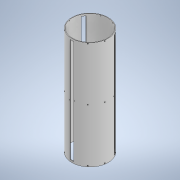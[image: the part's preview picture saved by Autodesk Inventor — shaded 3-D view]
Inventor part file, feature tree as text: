
AUTODESK INVENTOR PART (.ipt)
format: ipt  version: 2021 (Build 250183000, 183)  size: 350,208 bytes
history: native  units: in
note: dims shown in document units (in); Inventor stores cm internally (conversion verified against a paired STEP export)
features: other x34, hole x11, pattern_circular x8, sketch x8, plane x5, extrude x2
ambient origin geometry x8: Origin, YZ Plane, XZ Plane, XY Plane, X Axis, Y Axis, Z Axis, Center Point
bodies: Solid1 (feature_tree)
feature tree (68):
  extrude  "Extrusion1"  Depth=0.3937in
  plane  "Work Plane1"
  extrude  "Extrusion2"  Depth=0.3937in TaperAngle=0.0deg
  pattern_circular  "Circular Pattern1"  Count=3 Angle=360.0deg
  other  "Work Axis1"
  other  "Work Axis2"
  other  "Work Axis3"
  other  "Work Axis4"
  other  "Work Point1"
  other  "Work Point2"
  other  "Work Point3"
  other  "Central Plane"
  other  "Work Point4"
  other  "Work Axis6"
  other  "Work Axis7"
  other  "Offset Plane A"
  other  "Work Point5"
  other  "Work Point6"
  other  "Work Axis8"
  other  "Work Axis9"
  other  "Work Point7"
  other  "Work Point8"
  plane  "Work Plane5"
  plane  "Work Plane6"
  hole  "Hole1"  [1 undecoded]
  hole  "Hole2"  [1 undecoded]
  pattern_circular  "Circular Pattern3"  Count=3 Angle=360.0deg
  sketch  "Sketch5"  dims[d13=0.0484in d14=-11.811in]
  plane  "Work Plane7"
  sketch  "Sketch6"  dims[d15=0.0484in d16=0.1574in]
  hole  "Hole3"  [1 undecoded]
  other  "Work Axis10"
  hole  "Hole4"  [1 undecoded]
  pattern_circular  "Circular Pattern5"  Angle=60.0deg  [1 undecoded]
  plane  "Work Plane12"
  hole  "Hole5"  [1 undecoded]
  pattern_circular  "Circular Pattern6"  [2 undecoded]
  other  "plane for insert hole 1"
  sketch  "Sketch7"  dims[d17=-0.1574in]
  other  "plane for insert hole 2"
  sketch  "Sketch8"  dims[d48=1.0in d49=1.0in d29=0.096in d30=0.75in d31=0.185in d32=0.25in d33=0.5635in d34=1.0in d35=0.0in]
  hole  "insert hole 2"  [1 undecoded]
  hole  "insert hole 1"  [1 undecoded]
  pattern_circular  "Circular Pattern7"  [2 undecoded]
  pattern_circular  "Circular Pattern9"  [2 undecoded]
  other  "Work Axis14"
  other  "Work Axis16"
  other  "Work Point11"
  other  "Work Point12"
  other  "cap hardware plane 1"
  other  "cap hardware plane 2"
  sketch  "Sketch9"  dims[d52=1.0in d53=1.0in d38=0.096in d39=0.75in d40=0.185in d41=0.25in d42=0.5635in d43=1.0in d44=0.8108in d45=1.1811in d46=360.0deg]
  sketch  "Sketch10"  dims[d51=0.38in d54=0.177in d55=0.328in d56=0.332in d57=0.25in d58=0.5635in d59=0.484in d60=0.8108in d64=0.19in d65=0.177in d66=0.3229in d67=0.332in d68=0.25in d69=0.5635in d70=0.484in d71=0.8108in d72=1.5748in d73=360.0deg d75=60.0deg d76=1.0in d77=1.0in d78=0.129in d79=0.3229in d80=0.225in d81=0.25in d82=0.5635in d83=0.484in d84=0.8108in d85=1.1811in d86=360.0deg d88=0.2749in d89=0.2749in d90=0.0in d91=0.0in d92=0.0in d93=11.811in d94=0.0in d95=11.811in d96=0.129in d97=0.224in d98=0.225in d99=0.25in d100=0.5635in d101=0.349in d102=0.8108in d103=0.129in d104=0.224in d105=0.225in d106=0.25in d107=0.5635in d108=0.349in d109=0.8108in d110=1.1811in d111=360.0deg d116=1.1811in d117=360.0deg d119=0.0in d120=30.0deg d121=30.0deg d124=0.1969in d125=23.4252in d126=0.0in d127=0.0in d128=0.1969in d129=23.4252in d147=15.0deg d148=15.0deg d149=0.0in d150=0.0in d151=0.1969in d152=23.4252in d160=0.129in d161=0.75in d162=0.225in d163=0.25in d164=0.5635in d165=0.349in d166=0.8108in d167=0.129in d168=0.75in d169=0.225in d170=0.25in d171=0.5635in d172=0.349in d173=0.8108in d174=1.5748in d175=360.0deg d177=0.0in d178=0.0in d179=11.6142in d180=11.6142in d181=0.0in d182=0.0in d183=11.6142in d184=11.6142in d185=0.129in d186=0.75in d187=0.225in d188=0.25in d189=0.5635in d190=0.349in d191=0.8108in d192=0.129in d193=0.75in d194=0.225in d195=0.25in d196=0.5635in d197=0.349in d198=0.8108in d199=1.1811in d200=360.0deg d61=0.75in d62=0.8108in d63=0.0625in d130=1.0in d131=1.0in d132=1.0in d133=0.15in d134=0.25in d135=0.375in d136=0.5635in d137=0.75in d138=0.8108in d139=0.0625in d140=0.75in d141=0.375in]
  hole  "Quad Symmetry Holes 1"  [1 undecoded]
  hole  "Quad Symmetry Holes 2"  [1 undecoded]
  pattern_circular  "Circular Pattern11"  Count=30  [1 undecoded]
  hole  "Hole13"  [1 undecoded]
  hole  "Hole14"  [1 undecoded]
  pattern_circular  "Circular Pattern12"  [2 undecoded]
  sketch  "Sketch1"  dims[d3=0.0in d5=0.3937in]
  sketch  "Sketch2"  dims[d7=0.3937in d8=0.5in d9=0.0in d10=1.1811in d11=360.0deg]
  other  "Work Axis5"
  other  "Offset Plane B"
  other  "Work Axis11"
  other  "Work Axis12"
  other  "Work Point9"
  other  "Work Axis13"
  other  "Work Point10"
note: 21 required parameter values undecoded (feature->parameter linkage not recoverable at this tier; creation-order binding heuristic only, values carry confidence <= 0.55)
